# Revit family: Контейнерный шкаф «Модуль XL» Арт 13885
name_source: partatom
category: Антураж
revit_build: Autodesk Revit 2018 (Build: 20180423_1000(x64)
units: mm (PartAtom-declared; Revit-internal decimal feet)

## family parameters
Всегда вертикально = Да
Источник визуального образа = Геометрия семейства
На основе рабочей плоскости = Нет
Общий = Нет
При загрузке вырезать с полостями = Нет
Точка расчета площади = Нет

## types (2) — shared parameters
URL = https://hobbyka.ru
Артикул товара = Арт. 13885
Высота = 1540 мм
Группа модели = Контейнерные площадки для ТБО
Длина = 1530 мм
Изготовитель = ООО «Хоббика»
Изображение типоразмера = Контейнерный шкаф «Модуль XL» Арт 13885.jpg
Материал изделия = Сталь, дерево
Цвет каркаса = Сталь
Ширина = 1290 мм

## per-type parameters (varying)
| type | Версия "Лиственница" | Версия "Сосна" | Описание | Цвет отделки |
| Версия "Лиственница" | Да | Нет | Контейнерный шкаф «Модуль XL». Версия «Лиственница» | Лиственница |
| Версия "Сосна" | Нет | Да | Контейнерный шкаф «Модуль XL». Версия «Сосна» | Сосна |
